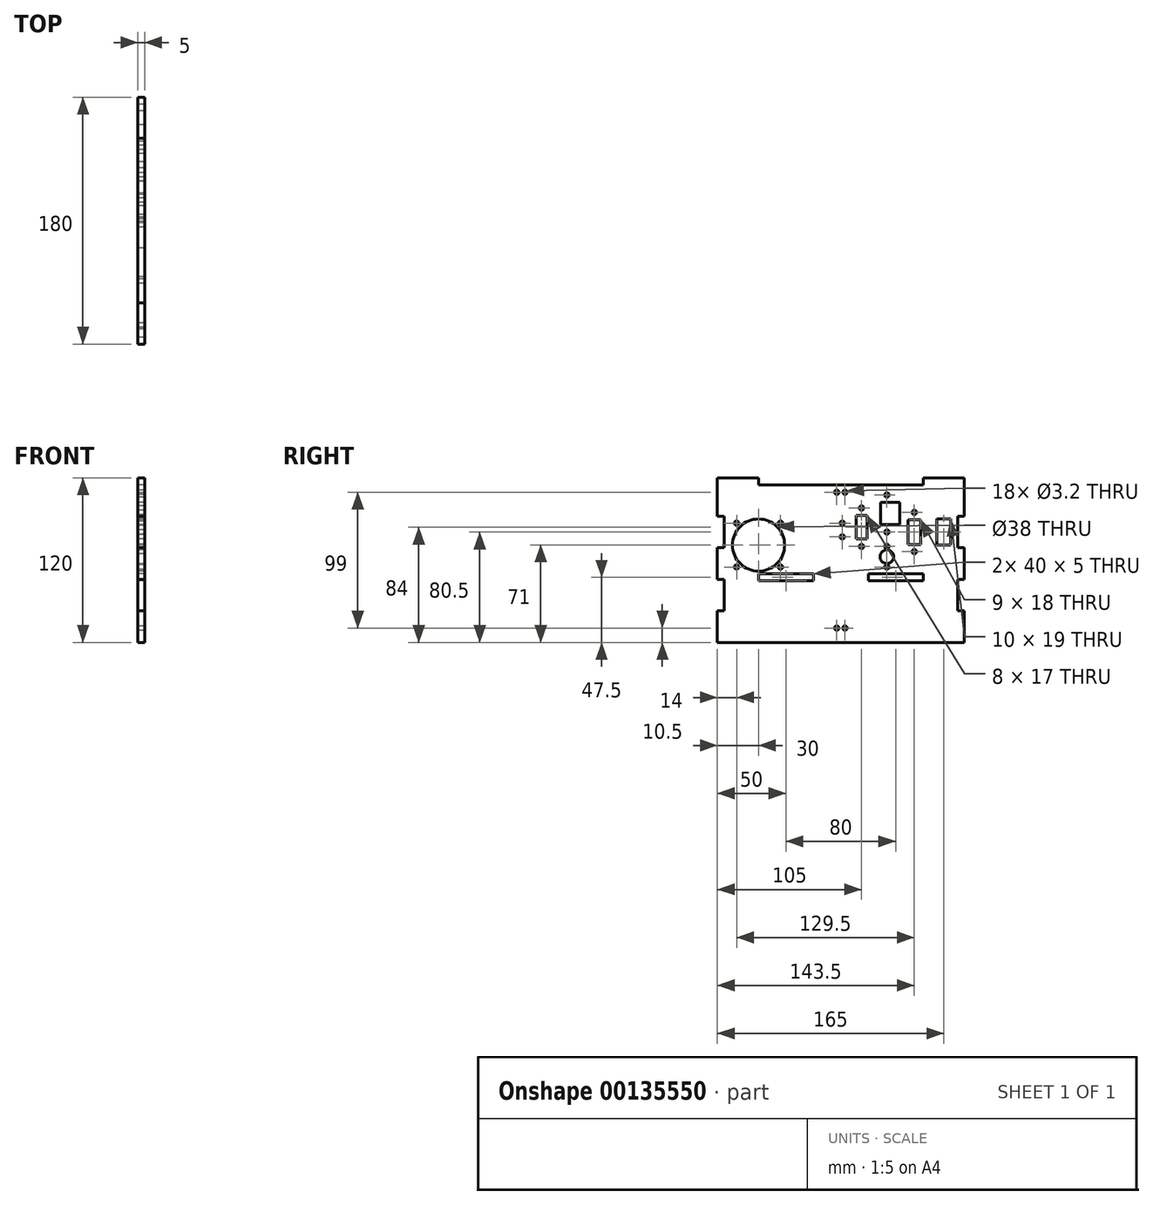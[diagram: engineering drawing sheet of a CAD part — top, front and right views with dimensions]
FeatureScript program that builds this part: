
annotation { "Feature Type Name" : "Feature", "Feature Type Description" : "" }
export const myFeature = defineFeature(function(context is Context, id is Id, definition is map)
    precondition{}
    {
        {
            var Q0;
            Q0=qCreatedBy(makeId("Right.planeOp"),FACE);
            var sketch = newSketch(context, id + "F0", { "sketchPlane" : qUnion([Q0])});
            skLineSegment(sketch, "E0", {"start": v(100, 0) * mm, "end": v(-100, 0) * mm, "construction": true});
            skLineSegment(sketch, "E1", {"start": v(0, 75) * mm, "end": v(0, -75) * mm, "construction": true});
            skLineSegment(sketch, "E2.bottom", {"start": v(90, 60) * mm, "end": v(60, 60) * mm});
            skLineSegment(sketch, "E2.top", {"start": v(90, -60) * mm, "end": v(-90, -60) * mm});
            skLineSegment(sketch, "E2.left", {"start": v(90, 60) * mm, "end": v(90, 32) * mm});
            skLineSegment(sketch, "E2.right", {"start": v(-90, 60) * mm, "end": v(-90, 32) * mm});
            skLineSegment(sketch, "E3", {"start": v(93.18, -10) * mm, "end": v(-93.18, -10) * mm, "construction": true});
            skLineSegment(sketch, "E4.bottom", {"start": v(85, 55) * mm, "end": v(-85, 55) * mm, "construction": true});
            skLineSegment(sketch, "E4.top", {"start": v(85, -55) * mm, "end": v(-85, -55) * mm, "construction": true});
            skLineSegment(sketch, "E4.left", {"start": v(85, 55) * mm, "end": v(85, -55) * mm, "construction": true});
            skLineSegment(sketch, "E4.right", {"start": v(-85, 55) * mm, "end": v(-85, -55) * mm, "construction": true});
            skLineSegment(sketch, "E5", {"start": v(-93.25, -15) * mm, "end": v(93.25, -15) * mm, "construction": true});
            skPoint(sketch, "E6", {"position": v(0, 0) * mm});
            skLineSegment(sketch, "E7", {"start": v(102.57, 10) * mm, "end": v(-105.44, 10) * mm, "construction": true});
            skLineSegment(sketch, "E8", {"start": v(60, 60) * mm, "end": v(60, 55) * mm});
            skLineSegment(sketch, "E9", {"start": v(-60, 60) * mm, "end": v(-60, 55) * mm});
            skLineSegment(sketch, "E10", {"start": v(60, 55) * mm, "end": v(-60, 55) * mm});
            skLineSegment(sketch, "E11", {"start": v(-90, -37) * mm, "end": v(-85, -37) * mm});
            skLineSegment(sketch, "E12.direction1", {"start": v(-90, -37) * mm, "end": v(-115, -37) * mm, "construction": true});
            skLineSegment(sketch, "E13", {"start": v(-85, -37) * mm, "end": v(-85, -14) * mm});
            skLineSegment(sketch, "E14", {"start": v(-85, 9) * mm, "end": v(-85, 32) * mm});
            skLineSegment(sketch, "E15.trimOffspring", {"start": v(-90, -37) * mm, "end": v(-90, -60) * mm});
            skLineSegment(sketch, "E16.trimOffspring", {"start": v(-90, 9) * mm, "end": v(-90, -14) * mm});
            skLineSegment(sketch, "E17.0.1.0", {"start": v(-90, -14) * mm, "end": v(-85, -14) * mm});
            skLineSegment(sketch, "E17.0.2.0", {"start": v(-90, 9) * mm, "end": v(-85, 9) * mm});
            skLineSegment(sketch, "E17.0.3.0", {"start": v(-90, 32) * mm, "end": v(-85, 32) * mm});
            skLineSegment(sketch, "E17.direction2", {"start": v(-90, -37) * mm, "end": v(-90, -14) * mm, "construction": true});
            skLineSegment(sketch, "E18", {"start": v(90, -37) * mm, "end": v(85, -37) * mm});
            skLineSegment(sketch, "E19.trimOffspring", {"start": v(90, -37) * mm, "end": v(90, -60) * mm});
            skLineSegment(sketch, "E20", {"start": v(85, -37) * mm, "end": v(85, -23.47) * mm});
            skLineSegment(sketch, "E21.0.1.0", {"start": v(90, -14) * mm, "end": v(85, -14) * mm});
            skLineSegment(sketch, "E21.0.2.0", {"start": v(90, 9) * mm, "end": v(85, 9) * mm});
            skLineSegment(sketch, "E21.0.3.0", {"start": v(90, 32) * mm, "end": v(85, 32) * mm});
            skLineSegment(sketch, "E21.direction1", {"start": v(85, -37) * mm, "end": v(110, -37) * mm, "construction": true});
            skLineSegment(sketch, "E21.direction2", {"start": v(85, -37) * mm, "end": v(85, -14) * mm, "construction": true});
            skLineSegment(sketch, "E22", {"start": v(85, 32) * mm, "end": v(85, 9) * mm});
            skLineSegment(sketch, "E23", {"start": v(85, -23.47) * mm, "end": v(85, -14) * mm});
            skLineSegment(sketch, "E24.trimOffspring", {"start": v(90, 9) * mm, "end": v(90, -14) * mm});
            skLineSegment(sketch, "E25.trimOffspring", {"start": v(-60, 60) * mm, "end": v(-90, 60) * mm});
            skLineSegment(sketch, "E26", {"start": v(85, 49.5) * mm, "end": v(-85, 49.5) * mm, "construction": true});
            skCircle(sketch, "E27", {"center": v(3, 49.5) * mm, "radius": 1.6 * mm});
            skCircle(sketch, "E28", {"center": v(-3, 49.5) * mm, "radius": 1.6 * mm});
            skLineSegment(sketch, "E29", {"start": v(62, 55) * mm, "end": v(62, -60) * mm, "construction": true});
            skLineSegment(sketch, "E30", {"start": v(80, 55) * mm, "end": v(80, -10) * mm, "construction": true});
            skLineSegment(sketch, "E31", {"start": v(70, 55) * mm, "end": v(70, -10) * mm, "construction": true});
            skLineSegment(sketch, "E32", {"start": v(80, 6) * mm, "end": v(70, 6) * mm, "construction": true});
            skLineSegment(sketch, "E33.bottom", {"start": v(80, 30) * mm, "end": v(70, 30) * mm});
            skLineSegment(sketch, "E33.top", {"start": v(80, 11) * mm, "end": v(70, 11) * mm});
            skLineSegment(sketch, "E33.left", {"start": v(80, 30) * mm, "end": v(80, 11) * mm});
            skLineSegment(sketch, "E33.right", {"start": v(70, 30) * mm, "end": v(70, 11) * mm});
            skLineSegment(sketch, "E34.bottom", {"start": v(60, -10) * mm, "end": v(20, -10) * mm});
            skLineSegment(sketch, "E34.top", {"start": v(60, -15) * mm, "end": v(20, -15) * mm});
            skLineSegment(sketch, "E34.left", {"start": v(60, -10) * mm, "end": v(60, -15) * mm});
            skLineSegment(sketch, "E34.right", {"start": v(20, -10) * mm, "end": v(20, -15) * mm});
            skLineSegment(sketch, "E35.bottom", {"start": v(-20, -10) * mm, "end": v(-60, -10) * mm});
            skLineSegment(sketch, "E35.top", {"start": v(-20, -15) * mm, "end": v(-60, -15) * mm});
            skLineSegment(sketch, "E35.left", {"start": v(-20, -10) * mm, "end": v(-20, -15) * mm});
            skLineSegment(sketch, "E35.right", {"start": v(-60, -10) * mm, "end": v(-60, -15) * mm});
            skLineSegment(sketch, "E36", {"start": v(80, 20.5) * mm, "end": v(70, 20.5) * mm, "construction": true});
            skLineSegment(sketch, "E37", {"start": v(85, -49.5) * mm, "end": v(-85, -49.5) * mm, "construction": true});
            skCircle(sketch, "E38", {"center": v(3, -49.5) * mm, "radius": 1.6 * mm});
            skCircle(sketch, "E39.MirrorC", {"center": v(-3, -49.5) * mm, "radius": 1.6 * mm});
            skSolve(sketch);
        }
        {
            var Q0;
            Q0=makeQuery(id+"F0.imprint","IMPRINT",FACE,{"disambiguationData":[TD([[makeQuery(id+"F0.imprint","IMPRINT",EDGE,{"derivedFrom":sQuery(id+"F0.wireOp",EDGE,"E2.bottom")}),1.0]])]});
            var sketch = newSketch(context, id + "F1", { "sketchPlane" : qUnion([Q0])});
            skLineSegment(sketch, "E40", {"start": v(53.5, 40.5) * mm, "end": v(53.5, -22.47) * mm, "construction": true});
            skLineSegment(sketch, "E41", {"start": v(48.45, 20.5) * mm, "end": v(33.5, 20.5) * mm, "construction": true});
            skPoint(sketch, "E42", {"position": v(53.5, 20.5) * mm});
            skCircle(sketch, "E43", {"center": v(53.5, 34.8) * mm, "radius": 1.6 * mm});
            skCircle(sketch, "E44", {"center": v(53.5, 6.2) * mm, "radius": 1.6 * mm});
            skLineSegment(sketch, "E45.bottom", {"start": v(58, 29.5) * mm, "end": v(49, 29.5) * mm});
            skLineSegment(sketch, "E45.top", {"start": v(58, 11.5) * mm, "end": v(49, 11.5) * mm});
            skLineSegment(sketch, "E45.left", {"start": v(58, 29.5) * mm, "end": v(58, 11.5) * mm});
            skLineSegment(sketch, "E45.right", {"start": v(49, 29.5) * mm, "end": v(49, 11.5) * mm});
            skLineSegment(sketch, "E46.bottom", {"start": v(60, 40.5) * mm, "end": v(47, 40.5) * mm, "construction": true});
            skLineSegment(sketch, "E46.top", {"start": v(60, 0.5) * mm, "end": v(47, 0.5) * mm, "construction": true});
            skLineSegment(sketch, "E46.left", {"start": v(60, 40.5) * mm, "end": v(60, 0.5) * mm, "construction": true});
            skLineSegment(sketch, "E46.right", {"start": v(47, 40.5) * mm, "end": v(47, 0.5) * mm, "construction": true});
            skSolve(sketch);
        }
        {
            var Q0;
            Q0=makeQuery(id+"F0.imprint","IMPRINT",FACE,{"disambiguationData":[TD([[makeQuery(id+"F0.imprint","IMPRINT",EDGE,{"derivedFrom":sQuery(id+"F0.wireOp",EDGE,"E2.bottom")}),1.0]])]});
            var sketch = newSketch(context, id + "F2", { "sketchPlane" : qUnion([Q0])});
            skLineSegment(sketch, "E47", {"start": v(33.5, 54) * mm, "end": v(33.5, -15.32) * mm, "construction": true});
            skLineSegment(sketch, "E48", {"start": v(60.5, 34) * mm, "end": v(2, 34) * mm, "construction": true});
            skPoint(sketch, "E49", {"position": v(33.5, 34) * mm});
            skCircle(sketch, "E50", {"center": v(33.5, 47.5) * mm, "radius": 1.6 * mm});
            skCircle(sketch, "E51.MirrorC", {"center": v(33.5, 20.5) * mm, "radius": 1.6 * mm});
            skLineSegment(sketch, "E52.bottom", {"start": v(43, 42) * mm, "end": v(29, 42) * mm});
            skLineSegment(sketch, "E52.top", {"start": v(43, 26) * mm, "end": v(29, 26) * mm});
            skLineSegment(sketch, "E52.left", {"start": v(43, 42) * mm, "end": v(43, 26) * mm});
            skLineSegment(sketch, "E52.right", {"start": v(29, 42) * mm, "end": v(29, 26) * mm});
            skLineSegment(sketch, "E53.bottom", {"start": v(45, 53) * mm, "end": v(22, 53) * mm, "construction": true});
            skLineSegment(sketch, "E53.top", {"start": v(45, 15) * mm, "end": v(22, 15) * mm, "construction": true});
            skLineSegment(sketch, "E53.left", {"start": v(45, 53) * mm, "end": v(45, 15) * mm, "construction": true});
            skLineSegment(sketch, "E53.right", {"start": v(22, 53) * mm, "end": v(22, 15) * mm, "construction": true});
            skSolve(sketch);
        }
        {
            var Q0;
            Q0=makeQuery(id+"F0.imprint","IMPRINT",FACE,{"disambiguationData":[TD([[makeQuery(id+"F0.imprint","IMPRINT",EDGE,{"derivedFrom":sQuery(id+"F0.wireOp",EDGE,"E2.bottom")}),1.0]])]});
            var sketch = newSketch(context, id + "F3", { "sketchPlane" : qUnion([Q0])});
            skLineSegment(sketch, "E54", {"start": v(33.5, 9.18) * mm, "end": v(33.5, -4.18) * mm, "construction": true});
            skLineSegment(sketch, "E55", {"start": v(39.27, 2.5) * mm, "end": v(27.73, 2.5) * mm, "construction": true});
            skPoint(sketch, "E56", {"position": v(33.5, 2.5) * mm});
            skPoint(sketch, "E57", {"position": v(33.5, 9.18) * mm});
            skPoint(sketch, "E58", {"position": v(33.5, -4.18) * mm});
            skPoint(sketch, "E59", {"position": v(27.73, 2.5) * mm});
            skPoint(sketch, "E60", {"position": v(39.27, 2.5) * mm});
            skCircle(sketch, "E61", {"center": v(33.5, 10) * mm, "radius": 1.6 * mm});
            skCircle(sketch, "E62.MirrorC", {"center": v(33.5, -5) * mm, "radius": 1.6 * mm});
            skCircle(sketch, "E63", {"center": v(33.5, 2.5) * mm, "radius": 5 * mm});
            skSolve(sketch);
        }
        {
            var Q0;
            Q0=makeQuery(id+"F0.imprint","IMPRINT",FACE,{"disambiguationData":[TD([[makeQuery(id+"F0.imprint","IMPRINT",EDGE,{"derivedFrom":sQuery(id+"F0.wireOp",EDGE,"E2.bottom")}),1.0]])]});
            var sketch = newSketch(context, id + "F4", { "sketchPlane" : qUnion([Q0])});
            skLineSegment(sketch, "E64.bottom", {"start": v(-40, 31) * mm, "end": v(-80, 31) * mm, "construction": true});
            skLineSegment(sketch, "E64.top", {"start": v(-40, -9) * mm, "end": v(-80, -9) * mm, "construction": true});
            skLineSegment(sketch, "E64.left", {"start": v(-40, 31) * mm, "end": v(-40, -9) * mm, "construction": true});
            skLineSegment(sketch, "E64.right", {"start": v(-80, 31) * mm, "end": v(-80, -9) * mm, "construction": true});
            skLineSegment(sketch, "E65.bottom", {"start": v(-44, 27) * mm, "end": v(-76, 27) * mm, "construction": true});
            skLineSegment(sketch, "E65.top", {"start": v(-44, -5) * mm, "end": v(-76, -5) * mm, "construction": true});
            skLineSegment(sketch, "E65.left", {"start": v(-44, 27) * mm, "end": v(-44, -5) * mm, "construction": true});
            skLineSegment(sketch, "E65.right", {"start": v(-76, 27) * mm, "end": v(-76, -5) * mm, "construction": true});
            skLineSegment(sketch, "E66", {"start": v(-60, 31) * mm, "end": v(-60, -9) * mm, "construction": true});
            skLineSegment(sketch, "E67", {"start": v(-40, 11) * mm, "end": v(-80, 11) * mm, "construction": true});
            skCircle(sketch, "E68", {"center": v(-60, 11) * mm, "radius": 19 * mm});
            skCircle(sketch, "E69", {"center": v(-44, 27) * mm, "radius": 1.6 * mm});
            skCircle(sketch, "E70", {"center": v(-76, 27) * mm, "radius": 1.6 * mm});
            skCircle(sketch, "E71", {"center": v(-76, -5) * mm, "radius": 1.6 * mm});
            skCircle(sketch, "E72", {"center": v(-44, -5) * mm, "radius": 1.6 * mm});
            skSolve(sketch);
        }
        {
            var Q0;
            Q0=makeQuery(id+"F0.imprint","IMPRINT",FACE,{"disambiguationData":[TD([[makeQuery(id+"F0.imprint","IMPRINT",EDGE,{"derivedFrom":sQuery(id+"F0.wireOp",EDGE,"E2.bottom")}),1.0]])]});
            var sketch = newSketch(context, id + "F5", { "sketchPlane" : qUnion([Q0])});
            skLineSegment(sketch, "E73.bottom", {"start": v(20, 41.5) * mm, "end": v(10, 41.5) * mm, "construction": true});
            skLineSegment(sketch, "E73.top", {"start": v(20, 6.5) * mm, "end": v(10, 6.5) * mm, "construction": true});
            skLineSegment(sketch, "E73.left", {"start": v(20, 41.5) * mm, "end": v(20, 6.5) * mm, "construction": true});
            skLineSegment(sketch, "E73.right", {"start": v(10, 41.5) * mm, "end": v(10, 6.5) * mm, "construction": true});
            skPoint(sketch, "E74.endSnap0", {"position": v(15, 6.5) * mm});
            skPoint(sketch, "E74.end.orphan", {"position": v(15, 6.5) * mm});
            skLineSegment(sketch, "E75", {"start": v(15, 6.5) * mm, "end": v(15, 41.5) * mm, "construction": true});
            skLineSegment(sketch, "E76", {"start": v(20, 24) * mm, "end": v(10, 24) * mm, "construction": true});
            skLineSegment(sketch, "E77.bottom", {"start": v(19, 32.5) * mm, "end": v(11, 32.5) * mm});
            skLineSegment(sketch, "E77.top", {"start": v(19, 15.5) * mm, "end": v(11, 15.5) * mm});
            skLineSegment(sketch, "E77.left", {"start": v(19, 32.5) * mm, "end": v(19, 15.5) * mm});
            skLineSegment(sketch, "E77.right", {"start": v(11, 32.5) * mm, "end": v(11, 15.5) * mm});
            skCircle(sketch, "E78", {"center": v(15, 38) * mm, "radius": 1.6 * mm});
            skCircle(sketch, "E79.MirrorC", {"center": v(15, 10) * mm, "radius": 1.6 * mm});
            skSolve(sketch);
        }
        {
            var Q0;
            Q0=makeQuery(id+"F0.imprint","IMPRINT",FACE,{"disambiguationData":[TD([[makeQuery(id+"F0.imprint","IMPRINT",EDGE,{"derivedFrom":sQuery(id+"F0.wireOp",EDGE,"E2.bottom")}),1.0]])]});
            var sketch = newSketch(context, id + "F6", { "sketchPlane" : qUnion([Q0])});
            skLineSegment(sketch, "E80.bottom", {"start": v(6, 40.5) * mm, "end": v(-4, 40.5) * mm, "construction": true});
            skLineSegment(sketch, "E80.top", {"start": v(6, -6.5) * mm, "end": v(-4, -6.5) * mm, "construction": true});
            skLineSegment(sketch, "E80.left", {"start": v(6, 40.5) * mm, "end": v(6, -6.5) * mm, "construction": true});
            skLineSegment(sketch, "E80.right", {"start": v(-4, 40.5) * mm, "end": v(-4, -6.5) * mm, "construction": true});
            skPoint(sketch, "E81.endSnap0", {"position": v(1, -6.5) * mm});
            skPoint(sketch, "E81.end.orphan", {"position": v(1, -6.5) * mm});
            skLineSegment(sketch, "E82", {"start": v(1, -11.5) * mm, "end": v(1, -6.5) * mm, "construction": true});
            skLineSegment(sketch, "E83", {"start": v(6, 17) * mm, "end": v(-4, 17) * mm, "construction": true});
            skCircle(sketch, "E84", {"center": v(1, 17) * mm, "radius": 1.6 * mm});
            skLineSegment(sketch, "E85.trimOffspring", {"start": v(1, -9.9) * mm, "end": v(1, 40.5) * mm, "construction": true});
            skPoint(sketch, "E86.center.orphan", {"position": v(1, 16.5) * mm});
            skCircle(sketch, "E87", {"center": v(1, 27) * mm, "radius": 1.6 * mm});
            skSolve(sketch);
        }
        {
            var Q0;
            Q0 = qSketchRegion(id + "F0", true);
            extrude(context, id + "F7", {"entities" : qUnion([Q0]), "depth" : 5 * mm});
        }
        {
            var Q0;
            Q0 = qSketchRegion(id + "F1", true);
            var Q1;
            Q1 = qSketchRegion(id + "F2", true);
            var Q2;
            Q2 = qSketchRegion(id + "F3", true);
            var Q3;
            Q3 = qSketchRegion(id + "F4", true);
            var Q4;
            Q4 = qSketchRegion(id + "F5", true);
            var Q5;
            Q5 = qSketchRegion(id + "F6", true);
            extrude(context, id + "F8", {"entities" : qUnion([Q0, Q1, Q2, Q3, Q4, Q5]), "operationType" : NewBodyOperationType.REMOVE, "depth" : 5 * mm});
        }
    });
